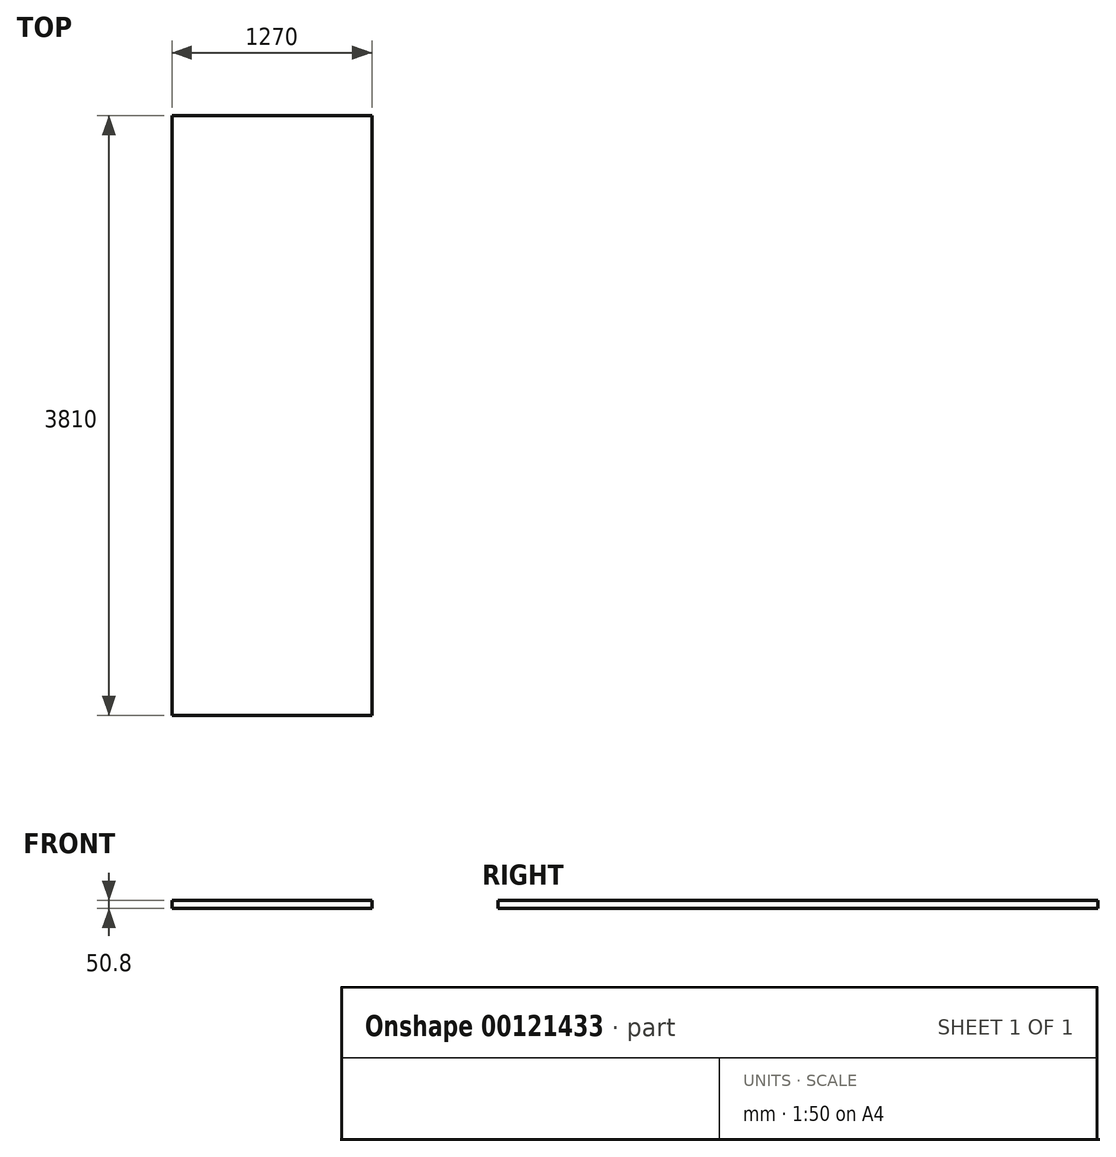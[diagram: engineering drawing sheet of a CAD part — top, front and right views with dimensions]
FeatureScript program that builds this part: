
annotation { "Feature Type Name" : "Feature", "Feature Type Description" : "" }
export const myFeature = defineFeature(function(context is Context, id is Id, definition is map)
    precondition{}
    {
        {
            var Q0;
            Q0=qCreatedBy(makeId("Top.planeOp"),FACE);
            var sketch = newSketch(context, id + "F0", { "sketchPlane" : qUnion([Q0])});
            skLineSegment(sketch, "E0.bottom", {"start": v(635, 1905) * mm, "end": v(-635, 1905) * mm});
            skLineSegment(sketch, "E0.top", {"start": v(635, -1905) * mm, "end": v(-635, -1905) * mm});
            skLineSegment(sketch, "E0.left", {"start": v(635, 1905) * mm, "end": v(635, -1905) * mm});
            skLineSegment(sketch, "E0.right", {"start": v(-635, 1905) * mm, "end": v(-635, -1905) * mm});
            skPoint(sketch, "E0.middle", {"position": v(0, 0) * mm});
            skSolve(sketch);
        }
        {
            var Q0;
            Q0=makeQuery(id+"F0.imprint","IMPRINT",FACE,{"disambiguationData":[TD([[makeQuery(id+"F0.imprint","IMPRINT",EDGE,{"derivedFrom":sQuery(id+"F0.wireOp",EDGE,"E0.bottom")}),1.0]])]});
            extrude(context, id + "F1", {"entities" : qUnion([Q0]), "depth" : 50.8 * mm});
        }
    });
